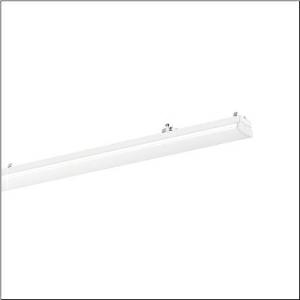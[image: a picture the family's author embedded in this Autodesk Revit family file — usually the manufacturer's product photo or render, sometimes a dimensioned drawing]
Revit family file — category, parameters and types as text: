
# Revit family: licross_21_recessed_opal_ho_52tl1ddv4l2m
name_source: partatom
category: Lighting Fixtures
units: mm (PartAtom-declared; Revit-internal decimal feet)

## family parameters
Cut with Voids When Loaded = No
Host = Face
Light Source = No
Part Type = Normal
Room Calculation Point = No
Round Connector Dimension = Use Diameter
Shared = No

## types (1)
- --- (1 x LED, 22050 lm, 125.6 W, 4000K)
    Apparent Load = 126 VA
    CIE Flux Codes = 44 73 91 87 100
    Color Rendering = 80
    Color Temperature = 4000K
    Default Elevation = 1800 mm
    Description = Licross 21 recessed opal HO, luminaire insert, of sheet steel, galvanised, coil coated, white, length: 2.250mm, width: 66mm, height: 67mm, LED rated luminous flux: 22.050lm, light colour: 840, SDCM (Standard Deviation of Colour Matching)MacAdam ≤ 3 SDCM (initial), control gear: DALI 2, with plug, 5-pole, with phase selection, mains connection: 220..240V, AC, 50/60Hz, rated input power: 126W, internal wiring halogen-free, primary optical cover: cover, of PMMA, light emission: direct with ceiling illumination distribution, primary light characteristic: symmetric, protection rating (complete): IP40, insulation class (complete): insulation class I (protective earthing), certification: CE, ENEC, VDE, UKCA, protection symbol: D if used in an environment without relevant dust loads with corresponding accessories, impact resistance: IK06, permissible ambient temperature for indoor applications: -40..+30°C, corresponds to IFS (International Featured Standards) requirements for safety and quality in the food industry, reducing of maximum allowable ambient temperature of 5°C with ceiling mounting, LABS conformity tested according to VDMA 24364:2018-05, The light source and the operating device comply with the requirements of the Ecodesign Regulation (EU) 2019/2020 and are replaceable in accordance with this regulation, packaging unit: 1 piece
    Height = 83 mm
    Lamp = 1 x LED
    Lamp Light Flux = 22050 lm
    Lamp Power = 125.6 W
    Lamp count = 1
    Length = 2250 mm
    Luminous efficacy = 176 lm/W
    Manufacturer = Siteco
    ModVariant = No
    Model = 52TL1DDV4L2M
    Mounting Place = Ceiling
    Mounting Type = Pendant
    Number of Poles = 1
    OnlyDefault = Yes
    Power Factor = 1
    Product Name = Licross 21 recessed opal HO
    Product group = luminaire insert | ceiling pendant
    ProductGroupID = 901
    Protection Class = Protection class I
    Protection Degree = IP 40
    RLX_Detail_Level = 1
    RLX_Emergency_Light_Flux = 0 lm
    RLX_Emergency_Type = 0
    RLX_Emergency_Type_DB = No
    RlxData = <blob elided: 27145 chars, md5=f933c2ae>
    Socket = socket
    Standby Power = 0 W
    System Light Flux = 22050 lm
    System Power = 126 W
    Type Comments = factory setting: luminous flux: 100 % | dim-lin: 254 | 489 mA
    Type Image = l_1313666.jpg
    URL = http://relux.com
    VarID = @adj_072523
    Voltage = 0 V
    Weight = 0.00 kg
    Width = 76 mm

## geometry (parser evidence)
native form markers: Blend x4, Sweep x14
no freeform markers — native parametric forms only
